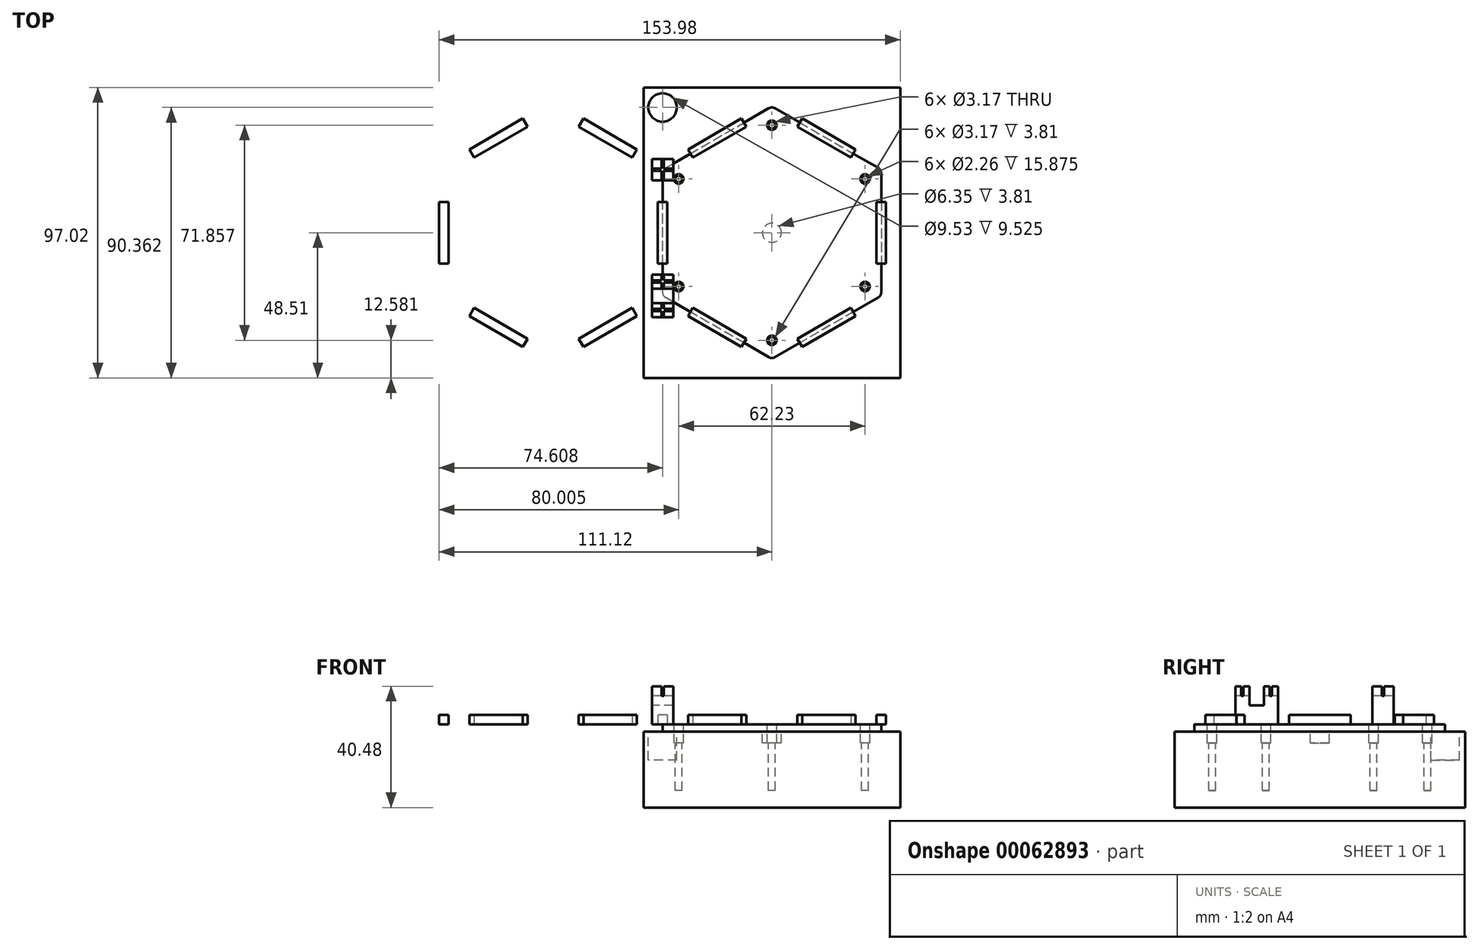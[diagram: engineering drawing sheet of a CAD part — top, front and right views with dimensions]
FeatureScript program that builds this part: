
annotation { "Feature Type Name" : "Feature", "Feature Type Description" : "" }
export const myFeature = defineFeature(function(context is Context, id is Id, definition is map)
    precondition{}
    {
        {
            var Q0;
            Q0=qCreatedBy(makeId("Top.planeOp"),FACE);
            var sketch = newSketch(context, id + "F0", { "sketchPlane" : qUnion([Q0])});
            skCircle(sketch, "E0.cCircle", {"center": v(0, 0) * mm, "radius": 36.51 * mm, "construction": true});
            skLineSegment(sketch, "E0.0", {"start": v(-36.51, 21.08) * mm, "end": v(0, 42.16) * mm});
            skLineSegment(sketch, "E0.1", {"start": v(0, 42.16) * mm, "end": v(36.51, 21.08) * mm});
            skLineSegment(sketch, "E0.2", {"start": v(36.51, 21.08) * mm, "end": v(36.51, -21.08) * mm});
            skLineSegment(sketch, "E0.3", {"start": v(36.51, -21.08) * mm, "end": v(0, -42.16) * mm});
            skLineSegment(sketch, "E0.4", {"start": v(0, -42.16) * mm, "end": v(-36.51, -21.08) * mm});
            skLineSegment(sketch, "E0.5", {"start": v(-36.51, -21.08) * mm, "end": v(-36.51, 21.08) * mm});
            skSolve(sketch);
        }
        {
            var Q0;
            Q0 = qSketchRegion(id + "F0", true);
            extrude(context, id + "F1", {"entities" : qUnion([Q0]), "depth" : 2.38 * mm});
        }
        {
            var Q0;
            Q0=makeQuery(id+"F1.opExtrude","CAP_FACE",FACE,{"disambiguationData":[OSD([sQuery(id+"F0.wireOp",EDGE,"E0.0"),sQuery(id+"F0.wireOp",EDGE,"E0.1"),sQuery(id+"F0.wireOp",EDGE,"E0.2"),sQuery(id+"F0.wireOp",EDGE,"E0.3"),sQuery(id+"F0.wireOp",EDGE,"E0.4"),sQuery(id+"F0.wireOp",EDGE,"E0.5")])],"isStart":false});
            var sketch = newSketch(context, id + "F2", { "sketchPlane" : qUnion([Q0])});
            skLineSegment(sketch, "E1.0", {"start": v(-31.12, -17.96) * mm, "end": v(-31.12, 17.96) * mm, "construction": true});
            skLineSegment(sketch, "E1.1", {"start": v(0, 35.93) * mm, "end": v(31.11, 17.96) * mm, "construction": true});
            skLineSegment(sketch, "E1.2", {"start": v(31.12, 17.96) * mm, "end": v(31.12, -17.96) * mm, "construction": true});
            skLineSegment(sketch, "E1.3", {"start": v(-31.12, 17.96) * mm, "end": v(0, 35.93) * mm, "construction": true});
            skLineSegment(sketch, "E1.4", {"start": v(31.12, -17.96) * mm, "end": v(0, -35.93) * mm, "construction": true});
            skLineSegment(sketch, "E1.5", {"start": v(0, -35.93) * mm, "end": v(-31.12, -17.96) * mm, "construction": true});
            skCircle(sketch, "E2", {"center": v(-31.12, 17.96) * mm, "radius": 1.59 * mm});
            skCircle(sketch, "E3", {"center": v(0, 35.93) * mm, "radius": 1.59 * mm});
            skCircle(sketch, "E4", {"center": v(31.11, 17.96) * mm, "radius": 1.59 * mm});
            skCircle(sketch, "E5", {"center": v(31.12, -17.96) * mm, "radius": 1.59 * mm});
            skCircle(sketch, "E6", {"center": v(0, -35.93) * mm, "radius": 1.59 * mm});
            skCircle(sketch, "E7", {"center": v(-31.12, -17.96) * mm, "radius": 1.59 * mm});
            skSolve(sketch);
        }
        {
            var Q0;
            Q0 = qSketchRegion(id + "F2", true);
            extrude(context, id + "F3", {"entities" : qUnion([Q0]), "operationType" : NewBodyOperationType.REMOVE, "endBound" : BoundingType.THROUGH_ALL, "oppositeDirection" : true, "depth" : 25.4 * mm});
        }
        {
            var Q0;
            Q0=makeQuery(id+"F1.opExtrude","SWEPT_EDGE",EDGE,{"disambiguationData":[OSD([sQuery(id+"F0.wireOp",EDGE,"E0.3"),sQuery(id+"F0.wireOp",EDGE,"E0.4")])]});
            var Q1;
            Q1=makeQuery(id+"F1.opExtrude","SWEPT_EDGE",EDGE,{"disambiguationData":[OSD([sQuery(id+"F0.wireOp",EDGE,"E0.2"),sQuery(id+"F0.wireOp",EDGE,"E0.3")])]});
            var Q2;
            Q2=makeQuery(id+"F1.opExtrude","SWEPT_EDGE",EDGE,{"disambiguationData":[OSD([sQuery(id+"F0.wireOp",EDGE,"E0.4"),sQuery(id+"F0.wireOp",EDGE,"E0.5")])]});
            var Q3;
            Q3=makeQuery(id+"F1.opExtrude","SWEPT_EDGE",EDGE,{"disambiguationData":[OSD([sQuery(id+"F0.wireOp",EDGE,"E0.0"),sQuery(id+"F0.wireOp",EDGE,"E0.5")])]});
            var Q4;
            Q4=makeQuery(id+"F1.opExtrude","SWEPT_EDGE",EDGE,{"disambiguationData":[OSD([sQuery(id+"F0.wireOp",EDGE,"E0.0"),sQuery(id+"F0.wireOp",EDGE,"E0.1")])]});
            var Q5;
            Q5=makeQuery(id+"F1.opExtrude","SWEPT_EDGE",EDGE,{"disambiguationData":[OSD([sQuery(id+"F0.wireOp",EDGE,"E0.1"),sQuery(id+"F0.wireOp",EDGE,"E0.2")])]});
            fillet(context, id + "F4", {"entities" : qUnion([Q0, Q1, Q2, Q3, Q4, Q5]), "radius" : 2 * mm, "tangentPropagation" : true, "allowEdgeOverflow" : false});
        }
        {
            var Q0;
            Q0=makeQuery(id+"F0.imprint","IMPRINT",FACE,{"disambiguationData":[TD([[makeQuery(id+"F0.imprint","IMPRINT",EDGE,{"derivedFrom":sQuery(id+"F0.wireOp",EDGE,"E0.0")}),-1.0]])]});
            var sketch = newSketch(context, id + "F5", { "sketchPlane" : qUnion([Q0])});
            skLineSegment(sketch, "E8.bottom", {"start": v(-42.86, -48.51) * mm, "end": v(42.86, -48.51) * mm});
            skLineSegment(sketch, "E8.top", {"start": v(-42.86, 48.51) * mm, "end": v(42.86, 48.51) * mm});
            skLineSegment(sketch, "E8.left", {"start": v(-42.86, -48.51) * mm, "end": v(-42.86, 48.51) * mm});
            skLineSegment(sketch, "E8.right", {"start": v(42.86, -48.51) * mm, "end": v(42.86, 48.51) * mm});
            skSolve(sketch);
        }
        {
            var Q0;
            Q0 = qSketchRegion(id + "F5", true);
            extrude(context, id + "F6", {"entities" : qUnion([Q0]), "oppositeDirection" : true, "depth" : 25.4 * mm});
        }
        {
            var Q0;
            Q0=makeQuery(id+"F6.opExtrude","CAP_FACE",FACE,{"disambiguationData":[OSD([sQuery(id+"F5.wireOp",EDGE,"E8.bottom"),sQuery(id+"F5.wireOp",EDGE,"E8.top"),sQuery(id+"F5.wireOp",EDGE,"E8.left"),sQuery(id+"F5.wireOp",EDGE,"E8.right")])],"isStart":true});
            var sketch = newSketch(context, id + "F7", { "sketchPlane" : qUnion([Q0])});
            skCircle(sketch, "E9", {"center": v(0, 0) * mm, "radius": 3.18 * mm});
            skCircle(sketch, "E10.0", {"center": v(0, -35.93) * mm, "radius": 1.59 * mm});
            skCircle(sketch, "E11.0", {"center": v(31.12, -17.96) * mm, "radius": 1.59 * mm});
            skCircle(sketch, "E12.0", {"center": v(-31.12, -17.96) * mm, "radius": 1.59 * mm});
            skCircle(sketch, "E13.0", {"center": v(-31.12, 17.96) * mm, "radius": 1.59 * mm});
            skCircle(sketch, "E14.0", {"center": v(0, 35.93) * mm, "radius": 1.59 * mm});
            skCircle(sketch, "E15.0", {"center": v(31.11, 17.96) * mm, "radius": 1.59 * mm});
            skSolve(sketch);
        }
        {
            var Q0;
            Q0 = qSketchRegion(id + "F7", true);
            extrude(context, id + "F8", {"entities" : qUnion([Q0]), "operationType" : NewBodyOperationType.REMOVE, "oppositeDirection" : true, "depth" : 3.8 * mm});
        }
        {
            var Q0;
            Q0=makeQuery(id+"F6.opExtrude","CAP_FACE",FACE,{"disambiguationData":[OSD([sQuery(id+"F5.wireOp",EDGE,"E8.bottom"),sQuery(id+"F5.wireOp",EDGE,"E8.top"),sQuery(id+"F5.wireOp",EDGE,"E8.left"),sQuery(id+"F5.wireOp",EDGE,"E8.right")])],"isStart":true});
            var sketch = newSketch(context, id + "F9", { "sketchPlane" : qUnion([Q0])});
            skCircle(sketch, "E16", {"center": v(0, -35.93) * mm, "radius": 1.13 * mm});
            skCircle(sketch, "E17.1.0", {"center": v(31.12, -17.96) * mm, "radius": 1.13 * mm});
            skCircle(sketch, "E17.2.0", {"center": v(31.11, 17.96) * mm, "radius": 1.13 * mm});
            skCircle(sketch, "E17.3.0", {"center": v(0, 35.93) * mm, "radius": 1.13 * mm});
            skCircle(sketch, "E17.4.0", {"center": v(-31.12, 17.96) * mm, "radius": 1.13 * mm});
            skCircle(sketch, "E17.5.0", {"center": v(-31.11, -17.96) * mm, "radius": 1.13 * mm});
            skPoint(sketch, "E17.center", {"position": v(0, 0) * mm});
            skSolve(sketch);
        }
        {
            var Q0;
            Q0 = qSketchRegion(id + "F9", true);
            extrude(context, id + "F10", {"entities" : qUnion([Q0]), "operationType" : NewBodyOperationType.REMOVE, "oppositeDirection" : true, "depth" : 19.68 * mm});
        }
        {
            var Q0;
            Q0=makeQuery(id+"F6.opExtrude","CAP_FACE",FACE,{"disambiguationData":[OSD([sQuery(id+"F5.wireOp",EDGE,"E8.bottom"),sQuery(id+"F5.wireOp",EDGE,"E8.top"),sQuery(id+"F5.wireOp",EDGE,"E8.left"),sQuery(id+"F5.wireOp",EDGE,"E8.right")])],"isStart":true});
            var sketch = newSketch(context, id + "F11", { "sketchPlane" : qUnion([Q0])});
            skCircle(sketch, "E18", {"center": v(-36.51, 41.85) * mm, "radius": 4.76 * mm});
            skLineSegment(sketch, "E19", {"start": v(-36.51, 41.85) * mm, "end": v(0, 41.85) * mm, "construction": true});
            skSolve(sketch);
        }
        {
            var Q0;
            Q0 = qSketchRegion(id + "F11", true);
            extrude(context, id + "F12", {"entities" : qUnion([Q0]), "operationType" : NewBodyOperationType.REMOVE, "oppositeDirection" : true, "depth" : 9.52 * mm});
        }
        {
            var Q0;
            Q0=makeQuery(id+"F1.opExtrude","CAP_FACE",FACE,{"disambiguationData":[OSD([sQuery(id+"F0.wireOp",EDGE,"E0.0"),sQuery(id+"F0.wireOp",EDGE,"E0.1"),sQuery(id+"F0.wireOp",EDGE,"E0.2"),sQuery(id+"F0.wireOp",EDGE,"E0.3"),sQuery(id+"F0.wireOp",EDGE,"E0.4"),sQuery(id+"F0.wireOp",EDGE,"E0.5")])],"isStart":false});
            var sketch = newSketch(context, id + "F13", { "sketchPlane" : qUnion([Q0])});
            skLineSegment(sketch, "E20.bottom", {"start": v(-34.93, 10.32) * mm, "end": v(-38.1, 10.32) * mm});
            skLineSegment(sketch, "E20.top", {"start": v(-34.93, -10.32) * mm, "end": v(-38.1, -10.32) * mm});
            skLineSegment(sketch, "E20.left", {"start": v(-34.93, 10.32) * mm, "end": v(-34.93, -10.32) * mm});
            skLineSegment(sketch, "E20.right", {"start": v(-38.1, 10.32) * mm, "end": v(-38.1, -10.32) * mm});
            skLineSegment(sketch, "E21", {"start": v(-36.51, 0) * mm, "end": v(-34.93, 0) * mm, "construction": true});
            skLineSegment(sketch, "E22", {"start": v(-38.1, 0) * mm, "end": v(-36.51, 0) * mm, "construction": true});
            skLineSegment(sketch, "E23.1.0", {"start": v(-27.99, -27.84) * mm, "end": v(-10.11, -38.15) * mm});
            skLineSegment(sketch, "E23.1.1", {"start": v(-26.4, -25.09) * mm, "end": v(-8.53, -35.4) * mm});
            skLineSegment(sketch, "E23.1.2", {"start": v(-8.53, -35.4) * mm, "end": v(-10.11, -38.15) * mm});
            skLineSegment(sketch, "E23.1.3", {"start": v(-26.4, -25.09) * mm, "end": v(-27.99, -27.84) * mm});
            skLineSegment(sketch, "E23.1.4", {"start": v(-19.05, -33) * mm, "end": v(-18.26, -31.62) * mm, "construction": true});
            skLineSegment(sketch, "E23.1.5", {"start": v(-18.26, -31.62) * mm, "end": v(-17.46, -30.25) * mm, "construction": true});
            skLineSegment(sketch, "E23.2.0", {"start": v(10.11, -38.15) * mm, "end": v(27.99, -27.84) * mm});
            skLineSegment(sketch, "E23.2.1", {"start": v(8.53, -35.4) * mm, "end": v(26.4, -25.09) * mm});
            skLineSegment(sketch, "E23.2.2", {"start": v(26.4, -25.09) * mm, "end": v(27.99, -27.84) * mm});
            skLineSegment(sketch, "E23.2.3", {"start": v(8.53, -35.4) * mm, "end": v(10.11, -38.15) * mm});
            skLineSegment(sketch, "E23.2.4", {"start": v(19.05, -33) * mm, "end": v(18.26, -31.62) * mm, "construction": true});
            skLineSegment(sketch, "E23.2.5", {"start": v(18.26, -31.62) * mm, "end": v(17.46, -30.25) * mm, "construction": true});
            skLineSegment(sketch, "E23.3.0", {"start": v(38.1, -10.32) * mm, "end": v(38.1, 10.32) * mm});
            skLineSegment(sketch, "E23.3.1", {"start": v(34.93, -10.32) * mm, "end": v(34.93, 10.32) * mm});
            skLineSegment(sketch, "E23.3.2", {"start": v(34.93, 10.32) * mm, "end": v(38.1, 10.32) * mm});
            skLineSegment(sketch, "E23.3.3", {"start": v(34.93, -10.32) * mm, "end": v(38.1, -10.32) * mm});
            skLineSegment(sketch, "E23.3.4", {"start": v(38.1, 0) * mm, "end": v(36.51, 0) * mm, "construction": true});
            skLineSegment(sketch, "E23.3.5", {"start": v(36.51, 0) * mm, "end": v(34.93, 0) * mm, "construction": true});
            skLineSegment(sketch, "E23.4.0", {"start": v(27.99, 27.84) * mm, "end": v(10.11, 38.15) * mm});
            skLineSegment(sketch, "E23.4.1", {"start": v(26.4, 25.09) * mm, "end": v(8.53, 35.4) * mm});
            skLineSegment(sketch, "E23.4.2", {"start": v(8.53, 35.4) * mm, "end": v(10.11, 38.15) * mm});
            skLineSegment(sketch, "E23.4.3", {"start": v(26.4, 25.09) * mm, "end": v(27.99, 27.84) * mm});
            skLineSegment(sketch, "E23.4.4", {"start": v(19.05, 33) * mm, "end": v(18.26, 31.62) * mm, "construction": true});
            skLineSegment(sketch, "E23.4.5", {"start": v(18.26, 31.62) * mm, "end": v(17.46, 30.25) * mm, "construction": true});
            skLineSegment(sketch, "E23.5.0", {"start": v(-10.11, 38.15) * mm, "end": v(-27.99, 27.84) * mm});
            skLineSegment(sketch, "E23.5.1", {"start": v(-8.53, 35.4) * mm, "end": v(-26.4, 25.09) * mm});
            skLineSegment(sketch, "E23.5.2", {"start": v(-26.4, 25.09) * mm, "end": v(-27.99, 27.84) * mm});
            skLineSegment(sketch, "E23.5.3", {"start": v(-8.53, 35.4) * mm, "end": v(-10.11, 38.15) * mm});
            skLineSegment(sketch, "E23.5.4", {"start": v(-19.05, 33) * mm, "end": v(-18.26, 31.62) * mm, "construction": true});
            skLineSegment(sketch, "E23.5.5", {"start": v(-18.26, 31.62) * mm, "end": v(-17.46, 30.25) * mm, "construction": true});
            skPoint(sketch, "E23.center", {"position": v(0, 0) * mm});
            skLineSegment(sketch, "E24.MirrorCS", {"start": v(-81.55, -35.4) * mm, "end": v(-83.14, -38.15) * mm});
            skLineSegment(sketch, "E25.MirrorCS", {"start": v(-64.5, 35.4) * mm, "end": v(-62.91, 38.15) * mm});
            skLineSegment(sketch, "E26.MirrorCS", {"start": v(-91.28, -31.62) * mm, "end": v(-90.49, -30.25) * mm, "construction": true});
            skLineSegment(sketch, "E27.MirrorCS", {"start": v(-64.5, -35.4) * mm, "end": v(-62.91, -38.15) * mm});
            skLineSegment(sketch, "E28.MirrorCS", {"start": v(-46.63, -25.09) * mm, "end": v(-45.04, -27.84) * mm});
            skLineSegment(sketch, "E29.MirrorCS", {"start": v(-54.77, -31.62) * mm, "end": v(-55.56, -30.25) * mm, "construction": true});
            skLineSegment(sketch, "E30.MirrorCS", {"start": v(-54.77, 31.62) * mm, "end": v(-55.56, 30.25) * mm, "construction": true});
            skLineSegment(sketch, "E31.MirrorCS", {"start": v(-81.55, 35.4) * mm, "end": v(-83.14, 38.15) * mm});
            skLineSegment(sketch, "E32.MirrorCS", {"start": v(-91.28, 31.62) * mm, "end": v(-90.49, 30.25) * mm, "construction": true});
            skLineSegment(sketch, "E33.MirrorCS", {"start": v(-99.42, -25.09) * mm, "end": v(-101.01, -27.84) * mm});
            skLineSegment(sketch, "E34.MirrorCS", {"start": v(-46.63, 25.09) * mm, "end": v(-45.04, 27.84) * mm});
            skLineSegment(sketch, "E35.MirrorCS", {"start": v(-99.42, 25.09) * mm, "end": v(-101.01, 27.84) * mm});
            skLineSegment(sketch, "E36.MirrorCS", {"start": v(-53.98, -33) * mm, "end": v(-54.77, -31.62) * mm, "construction": true});
            skLineSegment(sketch, "E37.MirrorCS", {"start": v(-92.08, 33) * mm, "end": v(-91.28, 31.62) * mm, "construction": true});
            skLineSegment(sketch, "E38.MirrorCS", {"start": v(-111.13, 0) * mm, "end": v(-109.54, 0) * mm, "construction": true});
            skLineSegment(sketch, "E39.MirrorCS", {"start": v(-53.98, 33) * mm, "end": v(-54.77, 31.62) * mm, "construction": true});
            skLineSegment(sketch, "E40.MirrorCS", {"start": v(-109.54, 0) * mm, "end": v(-107.95, 0) * mm, "construction": true});
            skLineSegment(sketch, "E41.MirrorCS", {"start": v(-92.08, -33) * mm, "end": v(-91.28, -31.62) * mm, "construction": true});
            skLineSegment(sketch, "E42.MirrorCS", {"start": v(-62.91, 38.15) * mm, "end": v(-45.04, 27.84) * mm});
            skLineSegment(sketch, "E43.MirrorCS", {"start": v(-107.95, -10.32) * mm, "end": v(-111.13, -10.32) * mm});
            skPoint(sketch, "E44.MirrorP", {"position": v(-73.03, 0) * mm});
            skLineSegment(sketch, "E45.MirrorCS", {"start": v(-45.04, -27.84) * mm, "end": v(-62.91, -38.15) * mm});
            skLineSegment(sketch, "E46.MirrorCS", {"start": v(-46.63, -25.09) * mm, "end": v(-64.5, -35.4) * mm});
            skLineSegment(sketch, "E47.MirrorCS", {"start": v(-83.14, -38.15) * mm, "end": v(-101.01, -27.84) * mm});
            skLineSegment(sketch, "E48.MirrorCS", {"start": v(-101.01, 27.84) * mm, "end": v(-83.14, 38.15) * mm});
            skLineSegment(sketch, "E49.MirrorCS", {"start": v(-64.5, 35.4) * mm, "end": v(-46.63, 25.09) * mm});
            skLineSegment(sketch, "E50.MirrorCS", {"start": v(-111.13, -10.32) * mm, "end": v(-111.13, 10.32) * mm});
            skLineSegment(sketch, "E51.MirrorCS", {"start": v(-99.42, 25.09) * mm, "end": v(-81.55, 35.4) * mm});
            skLineSegment(sketch, "E52.MirrorCS", {"start": v(-107.95, -10.32) * mm, "end": v(-107.95, 10.32) * mm});
            skLineSegment(sketch, "E53.MirrorCS", {"start": v(-107.95, 10.32) * mm, "end": v(-111.13, 10.32) * mm});
            skLineSegment(sketch, "E54.MirrorCS", {"start": v(-81.55, -35.4) * mm, "end": v(-99.42, -25.09) * mm});
            skSolve(sketch);
        }
        {
            var Q0;
            Q0 = qSketchRegion(id + "F13", true);
            extrude(context, id + "F14", {"entities" : qUnion([Q0]), "depth" : 3.17 * mm});
        }
        {
            var Q0;
            Q0=makeQuery(id+"F1.opExtrude","CAP_FACE",FACE,{"disambiguationData":[OSD([sQuery(id+"F0.wireOp",EDGE,"E0.0"),sQuery(id+"F0.wireOp",EDGE,"E0.1"),sQuery(id+"F0.wireOp",EDGE,"E0.2"),sQuery(id+"F0.wireOp",EDGE,"E0.3"),sQuery(id+"F0.wireOp",EDGE,"E0.4"),sQuery(id+"F0.wireOp",EDGE,"E0.5")])],"isStart":false});
            var sketch = newSketch(context, id + "F15", { "sketchPlane" : qUnion([Q0])});
            skLineSegment(sketch, "E55.bottom", {"start": v(-32.94, 24.65) * mm, "end": v(-40.08, 24.65) * mm});
            skLineSegment(sketch, "E55.top", {"start": v(-32.94, 17.5) * mm, "end": v(-40.08, 17.5) * mm});
            skLineSegment(sketch, "E55.left", {"start": v(-32.94, 24.65) * mm, "end": v(-32.94, 17.5) * mm});
            skLineSegment(sketch, "E55.right", {"start": v(-40.08, 24.65) * mm, "end": v(-40.08, 17.5) * mm});
            skPoint(sketch, "E55.middle", {"position": v(-36.51, 21.08) * mm});
            skCircle(sketch, "E56", {"center": v(-36.51, 21.08) * mm, "radius": 10.76 * mm, "construction": true});
            skLineSegment(sketch, "E57.bottom", {"start": v(-40.08, -13.94) * mm, "end": v(-32.94, -13.94) * mm});
            skLineSegment(sketch, "E57.top", {"start": v(-40.08, -28.22) * mm, "end": v(-32.94, -28.22) * mm});
            skLineSegment(sketch, "E57.left", {"start": v(-40.08, -13.94) * mm, "end": v(-40.08, -28.22) * mm});
            skLineSegment(sketch, "E57.right", {"start": v(-32.94, -13.94) * mm, "end": v(-32.94, -28.22) * mm});
            skPoint(sketch, "E57.middle", {"position": v(-36.51, -21.08) * mm});
            skCircle(sketch, "E58", {"center": v(-36.51, -21.08) * mm, "radius": 10.76 * mm, "construction": true});
            skSolve(sketch);
        }
        {
            var Q0;
            Q0 = qSketchRegion(id + "F15", true);
            extrude(context, id + "F16", {"entities" : qUnion([Q0]), "depth" : 12.7 * mm});
        }
        {
            var Q0;
            Q0=makeQuery(id+"F16.opExtrude","SWEPT_FACE",FACE,{"disambiguationData":[OSD([sQuery(id+"F15.wireOp",EDGE,"E57.left")])]});
            var sketch = newSketch(context, id + "F17", { "sketchPlane" : qUnion([Q0])});
            skLineSegment(sketch, "E59.bottom", {"start": v(18.7, 15.08) * mm, "end": v(23.46, 15.08) * mm});
            skLineSegment(sketch, "E59.top", {"start": v(18.7, 8.73) * mm, "end": v(23.46, 8.73) * mm});
            skLineSegment(sketch, "E59.left", {"start": v(18.7, 15.08) * mm, "end": v(18.7, 8.73) * mm});
            skLineSegment(sketch, "E59.right", {"start": v(23.46, 15.08) * mm, "end": v(23.46, 8.73) * mm});
            skLineSegment(sketch, "E60", {"start": v(18.7, 8.73) * mm, "end": v(13.94, 8.73) * mm, "construction": true});
            skLineSegment(sketch, "E61", {"start": v(23.46, 8.73) * mm, "end": v(28.22, 8.73) * mm, "construction": true});
            skSolve(sketch);
        }
        {
            var Q0;
            Q0 = qSketchRegion(id + "F17", true);
            extrude(context, id + "F18", {"entities" : qUnion([Q0]), "operationType" : NewBodyOperationType.REMOVE, "endBound" : BoundingType.UP_TO_NEXT, "oppositeDirection" : true, "depth" : 25.4 * mm});
        }
        {
            var Q0;
            Q0=makeQuery(id+"F16.opExtrude","CAP_FACE",FACE,{"disambiguationData":[OSD([sQuery(id+"F15.wireOp",EDGE,"E55.bottom"),sQuery(id+"F15.wireOp",EDGE,"E55.top"),sQuery(id+"F15.wireOp",EDGE,"E55.left"),sQuery(id+"F15.wireOp",EDGE,"E55.right")])],"isStart":false});
            var sketch = newSketch(context, id + "F19", { "sketchPlane" : qUnion([Q0])});
            skLineSegment(sketch, "E62.bottom", {"start": v(-36.9, 24.65) * mm, "end": v(-36.13, 24.65) * mm});
            skLineSegment(sketch, "E62.top", {"start": v(-36.9, 17.5) * mm, "end": v(-36.13, 17.5) * mm});
            skLineSegment(sketch, "E62.left", {"start": v(-36.9, 24.65) * mm, "end": v(-36.9, 17.5) * mm});
            skLineSegment(sketch, "E62.right", {"start": v(-36.13, 24.65) * mm, "end": v(-36.13, 17.5) * mm});
            skLineSegment(sketch, "E63.bottom", {"start": v(-32.94, 21.46) * mm, "end": v(-40.08, 21.46) * mm});
            skLineSegment(sketch, "E63.top", {"start": v(-32.94, 20.7) * mm, "end": v(-40.08, 20.7) * mm});
            skLineSegment(sketch, "E63.left", {"start": v(-32.94, 21.46) * mm, "end": v(-32.94, 20.7) * mm});
            skLineSegment(sketch, "E63.right", {"start": v(-40.08, 21.46) * mm, "end": v(-40.08, 20.7) * mm});
            skLineSegment(sketch, "E64", {"start": v(-40.08, 24.65) * mm, "end": v(-36.9, 21.46) * mm, "construction": true});
            skLineSegment(sketch, "E65", {"start": v(-36.13, 20.7) * mm, "end": v(-32.94, 17.5) * mm, "construction": true});
            skLineSegment(sketch, "E66", {"start": v(-36.13, 21.46) * mm, "end": v(-32.94, 24.65) * mm, "construction": true});
            skLineSegment(sketch, "E67.bottom", {"start": v(-36.9, -13.94) * mm, "end": v(-36.13, -13.94) * mm});
            skLineSegment(sketch, "E67.top", {"start": v(-36.9, -28.22) * mm, "end": v(-36.13, -28.22) * mm});
            skLineSegment(sketch, "E67.left", {"start": v(-36.9, -13.94) * mm, "end": v(-36.9, -28.22) * mm});
            skLineSegment(sketch, "E67.right", {"start": v(-36.13, -13.94) * mm, "end": v(-36.13, -28.22) * mm});
            skLineSegment(sketch, "E68.bottom", {"start": v(-32.94, -15.94) * mm, "end": v(-40.08, -15.94) * mm});
            skLineSegment(sketch, "E68.top", {"start": v(-32.94, -16.7) * mm, "end": v(-40.08, -16.7) * mm});
            skLineSegment(sketch, "E68.left", {"start": v(-32.94, -15.94) * mm, "end": v(-32.94, -16.7) * mm});
            skLineSegment(sketch, "E68.right", {"start": v(-40.08, -15.94) * mm, "end": v(-40.08, -16.7) * mm});
            skLineSegment(sketch, "E69.bottom", {"start": v(-32.94, -25.46) * mm, "end": v(-40.08, -25.46) * mm});
            skLineSegment(sketch, "E69.top", {"start": v(-32.94, -26.22) * mm, "end": v(-40.08, -26.22) * mm});
            skLineSegment(sketch, "E69.left", {"start": v(-32.94, -25.46) * mm, "end": v(-32.94, -26.22) * mm});
            skLineSegment(sketch, "E69.right", {"start": v(-40.08, -25.46) * mm, "end": v(-40.08, -26.22) * mm});
            skLineSegment(sketch, "E70", {"start": v(-36.9, -16.7) * mm, "end": v(-40.08, -18.7) * mm, "construction": true});
            skLineSegment(sketch, "E71", {"start": v(-36.9, -15.94) * mm, "end": v(-40.08, -13.94) * mm, "construction": true});
            skLineSegment(sketch, "E72", {"start": v(-36.13, -15.94) * mm, "end": v(-32.94, -13.94) * mm, "construction": true});
            skLineSegment(sketch, "E73", {"start": v(-36.13, -25.46) * mm, "end": v(-32.94, -23.46) * mm, "construction": true});
            skLineSegment(sketch, "E74", {"start": v(-36.13, -26.22) * mm, "end": v(-32.94, -28.22) * mm, "construction": true});
            skLineSegment(sketch, "E75", {"start": v(-36.9, -26.22) * mm, "end": v(-40.08, -28.22) * mm, "construction": true});
            skSolve(sketch);
        }
        {
            var Q0;
            Q0 = qSketchRegion(id + "F19", true);
            extrude(context, id + "F20", {"entities" : qUnion([Q0]), "operationType" : NewBodyOperationType.REMOVE, "oppositeDirection" : true, "depth" : 3.17 * mm});
        }
    });
